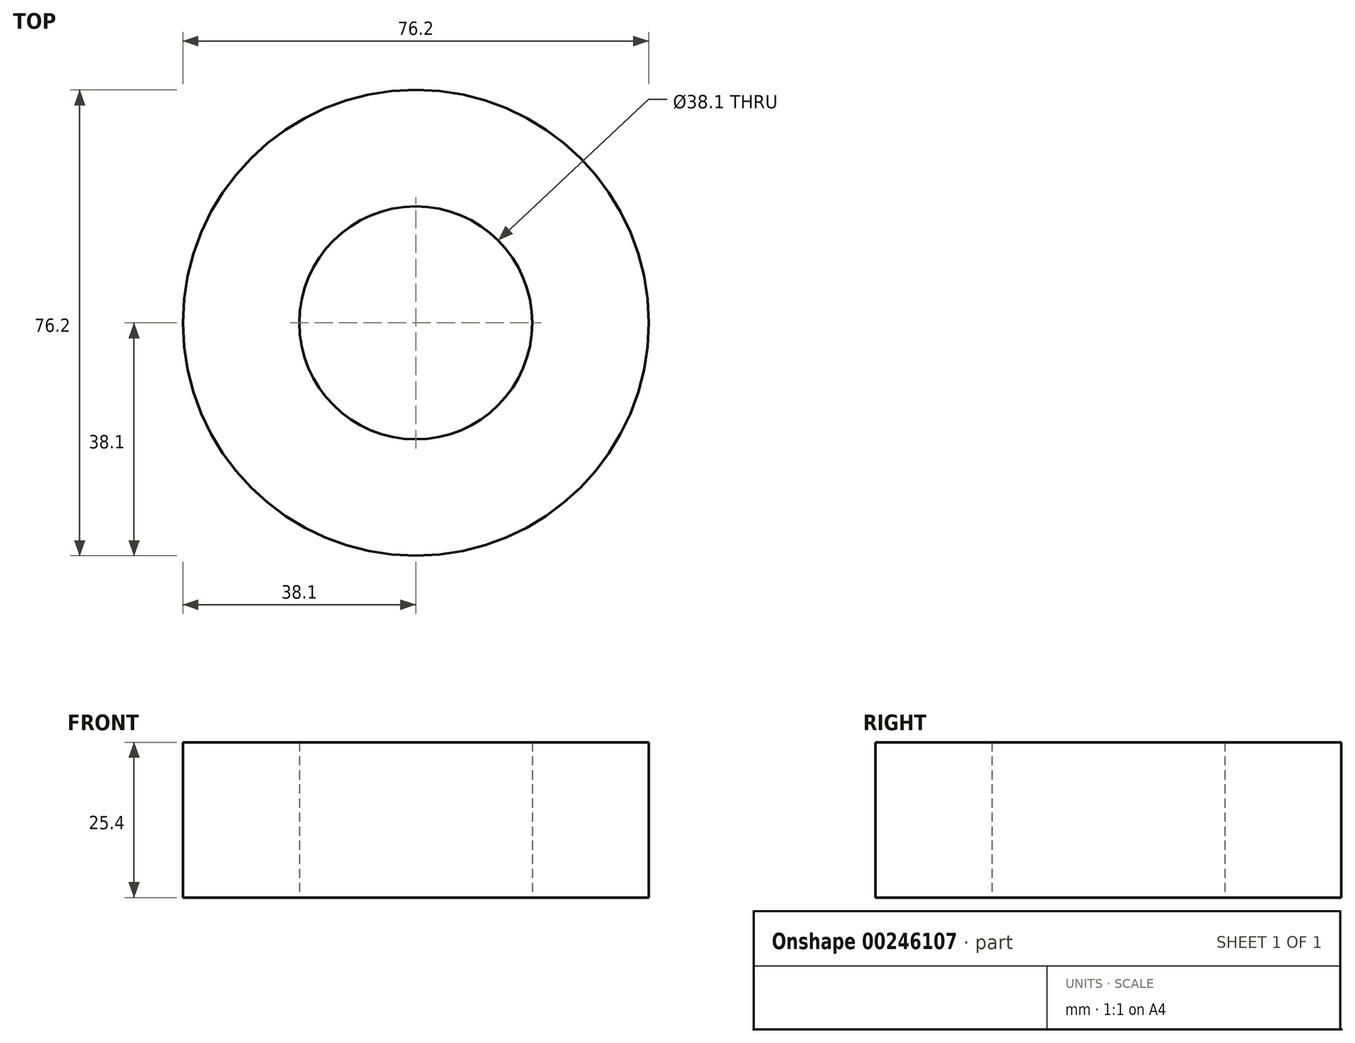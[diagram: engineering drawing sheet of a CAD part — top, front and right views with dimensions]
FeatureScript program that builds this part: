
annotation { "Feature Type Name" : "Feature", "Feature Type Description" : "" }
export const myFeature = defineFeature(function(context is Context, id is Id, definition is map)
    precondition{}
    {
        {
            var Q0;
            Q0=qCreatedBy(makeId("Top.planeOp"),FACE);
            var sketch = newSketch(context, id + "F0", { "sketchPlane" : qUnion([Q0])});
            skCircle(sketch, "E0", {"center": v(0, 0) * mm, "radius": 38.1 * mm});
            skCircle(sketch, "E1", {"center": v(0, 0) * mm, "radius": 31.75 * mm});
            skCircle(sketch, "E2", {"center": v(0, 0) * mm, "radius": 25.4 * mm});
            skCircle(sketch, "E3", {"center": v(0, 0) * mm, "radius": 19.05 * mm});
            skSolve(sketch);
        }
        {
            var Q0;
            Q0 = qSketchRegion(id + "F0", true);
            var Q1;
            Q1=makeQuery(id+"F0.imprint","IMPRINT",FACE,{"disambiguationData":[TD([[makeQuery(id+"F0.imprint","IMPRINT",EDGE,{"derivedFrom":sQuery(id+"F0.wireOp",EDGE,"E1")}),1.0]])]});
            var Q2;
            Q2=makeQuery(id+"F0.imprint","IMPRINT",FACE,{"disambiguationData":[TD([[makeQuery(id+"F0.imprint","IMPRINT",EDGE,{"derivedFrom":sQuery(id+"F0.wireOp",EDGE,"E2")}),1.0]])]});
            extrude(context, id + "F1", {"entities" : qUnion([Q0, Q1, Q2]), "depth" : 25.4 * mm});
        }
    });
